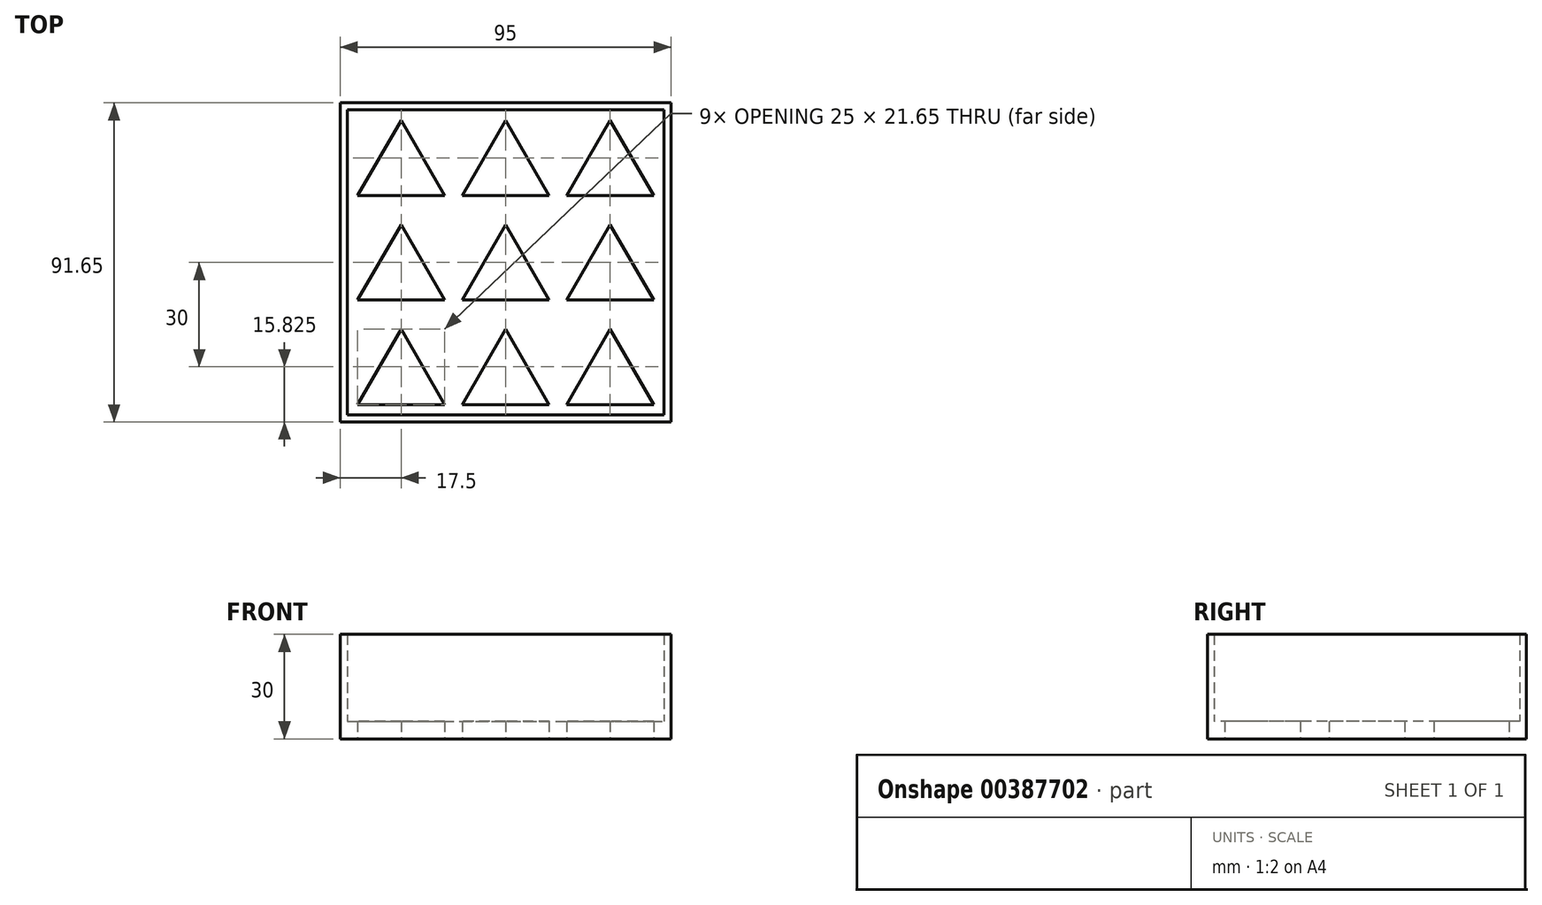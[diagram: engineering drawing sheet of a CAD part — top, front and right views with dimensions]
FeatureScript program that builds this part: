
annotation { "Feature Type Name" : "Feature", "Feature Type Description" : "" }
export const myFeature = defineFeature(function(context is Context, id is Id, definition is map)
    precondition{}
    {
        {
            var Q0;
            Q0=qCreatedBy(makeId("Top.planeOp"),FACE);
            var sketch = newSketch(context, id + "F0", { "sketchPlane" : qUnion([Q0])});
            skLineSegment(sketch, "E0", {"start": v(-12.5, 21.65) * mm, "end": v(-25, 0) * mm});
            skLineSegment(sketch, "E1", {"start": v(-25, 0) * mm, "end": v(0, 0) * mm});
            skLineSegment(sketch, "E2", {"start": v(0, 0) * mm, "end": v(-12.5, 21.65) * mm});
            skLineSegment(sketch, "E3.0.1.0", {"start": v(-25, 30) * mm, "end": v(0, 30) * mm});
            skLineSegment(sketch, "E3.0.1.1", {"start": v(-12.5, 51.65) * mm, "end": v(-25, 30) * mm});
            skLineSegment(sketch, "E3.0.1.2", {"start": v(0, 30) * mm, "end": v(-12.5, 51.65) * mm});
            skLineSegment(sketch, "E3.0.2.0", {"start": v(-25, 60) * mm, "end": v(0, 60) * mm});
            skLineSegment(sketch, "E3.0.2.1", {"start": v(-12.5, 81.65) * mm, "end": v(-25, 60) * mm});
            skLineSegment(sketch, "E3.0.2.2", {"start": v(0, 60) * mm, "end": v(-12.5, 81.65) * mm});
            skLineSegment(sketch, "E3.1.0.0", {"start": v(5, 0) * mm, "end": v(30, 0) * mm});
            skLineSegment(sketch, "E3.1.0.1", {"start": v(17.5, 21.65) * mm, "end": v(5, 0) * mm});
            skLineSegment(sketch, "E3.1.0.2", {"start": v(30, 0) * mm, "end": v(17.5, 21.65) * mm});
            skLineSegment(sketch, "E3.1.1.0", {"start": v(5, 30) * mm, "end": v(30, 30) * mm});
            skLineSegment(sketch, "E3.1.1.1", {"start": v(17.5, 51.65) * mm, "end": v(5, 30) * mm});
            skLineSegment(sketch, "E3.1.1.2", {"start": v(30, 30) * mm, "end": v(17.5, 51.65) * mm});
            skLineSegment(sketch, "E3.1.2.0", {"start": v(5, 60) * mm, "end": v(30, 60) * mm});
            skLineSegment(sketch, "E3.1.2.1", {"start": v(17.5, 81.65) * mm, "end": v(5, 60) * mm});
            skLineSegment(sketch, "E3.1.2.2", {"start": v(30, 60) * mm, "end": v(17.5, 81.65) * mm});
            skLineSegment(sketch, "E3.2.0.0", {"start": v(35, 0) * mm, "end": v(60, 0) * mm});
            skLineSegment(sketch, "E3.2.0.1", {"start": v(47.5, 21.65) * mm, "end": v(35, 0) * mm});
            skLineSegment(sketch, "E3.2.0.2", {"start": v(60, 0) * mm, "end": v(47.5, 21.65) * mm});
            skLineSegment(sketch, "E3.2.1.0", {"start": v(35, 30) * mm, "end": v(60, 30) * mm});
            skLineSegment(sketch, "E3.2.1.1", {"start": v(47.5, 51.65) * mm, "end": v(35, 30) * mm});
            skLineSegment(sketch, "E3.2.1.2", {"start": v(60, 30) * mm, "end": v(47.5, 51.65) * mm});
            skLineSegment(sketch, "E3.2.2.0", {"start": v(35, 60) * mm, "end": v(60, 60) * mm});
            skLineSegment(sketch, "E3.2.2.1", {"start": v(47.5, 81.65) * mm, "end": v(35, 60) * mm});
            skLineSegment(sketch, "E3.2.2.2", {"start": v(60, 60) * mm, "end": v(47.5, 81.65) * mm});
            skLineSegment(sketch, "E3.direction1", {"start": v(-25, 0) * mm, "end": v(5, 0) * mm, "construction": true});
            skLineSegment(sketch, "E3.direction2", {"start": v(-25, 0) * mm, "end": v(-25, 30) * mm, "construction": true});
            skLineSegment(sketch, "E4.bottom", {"start": v(-30, 86.65) * mm, "end": v(65, 86.65) * mm});
            skLineSegment(sketch, "E4.top", {"start": v(-30, -5) * mm, "end": v(65, -5) * mm});
            skLineSegment(sketch, "E4.left", {"start": v(-30, 86.65) * mm, "end": v(-30, -5) * mm});
            skLineSegment(sketch, "E4.right", {"start": v(65, 86.65) * mm, "end": v(65, -5) * mm});
            skSolve(sketch);
        }
        {
            var Q0;
            Q0 = qSketchRegion(id + "F0", true);
            extrude(context, id + "F1", {"entities" : qUnion([Q0]), "depth" : 5 * mm});
        }
        {
            var Q0;
            Q0=makeQuery(id+"F1.opExtrude","CAP_FACE",FACE,{"disambiguationData":[OSD([sQuery(id+"F0.wireOp",EDGE,"E0"),sQuery(id+"F0.wireOp",EDGE,"E1"),sQuery(id+"F0.wireOp",EDGE,"E2"),sQuery(id+"F0.wireOp",EDGE,"E3.0.1.0"),sQuery(id+"F0.wireOp",EDGE,"E3.0.1.1"),sQuery(id+"F0.wireOp",EDGE,"E3.0.1.2"),sQuery(id+"F0.wireOp",EDGE,"E3.0.2.0"),sQuery(id+"F0.wireOp",EDGE,"E3.0.2.1"),sQuery(id+"F0.wireOp",EDGE,"E3.0.2.2"),sQuery(id+"F0.wireOp",EDGE,"E3.1.0.0"),sQuery(id+"F0.wireOp",EDGE,"E3.1.0.1"),sQuery(id+"F0.wireOp",EDGE,"E3.1.0.2"),sQuery(id+"F0.wireOp",EDGE,"E3.1.1.0"),sQuery(id+"F0.wireOp",EDGE,"E3.1.1.1"),sQuery(id+"F0.wireOp",EDGE,"E3.1.1.2"),sQuery(id+"F0.wireOp",EDGE,"E3.1.2.0"),sQuery(id+"F0.wireOp",EDGE,"E3.1.2.1"),sQuery(id+"F0.wireOp",EDGE,"E3.1.2.2"),sQuery(id+"F0.wireOp",EDGE,"E3.2.0.0"),sQuery(id+"F0.wireOp",EDGE,"E3.2.0.1"),sQuery(id+"F0.wireOp",EDGE,"E3.2.0.2"),sQuery(id+"F0.wireOp",EDGE,"E3.2.1.0"),sQuery(id+"F0.wireOp",EDGE,"E3.2.1.1"),sQuery(id+"F0.wireOp",EDGE,"E3.2.1.2"),sQuery(id+"F0.wireOp",EDGE,"E3.2.2.0"),sQuery(id+"F0.wireOp",EDGE,"E3.2.2.1"),sQuery(id+"F0.wireOp",EDGE,"E3.2.2.2"),sQuery(id+"F0.wireOp",EDGE,"E4.bottom"),sQuery(id+"F0.wireOp",EDGE,"E4.top"),sQuery(id+"F0.wireOp",EDGE,"E4.left"),sQuery(id+"F0.wireOp",EDGE,"E4.right")])],"isStart":false});
            var sketch = newSketch(context, id + "F2", { "sketchPlane" : qUnion([Q0])});
            skLineSegment(sketch, "E5.0", {"start": v(-28, 84.65) * mm, "end": v(-28, -3) * mm});
            skLineSegment(sketch, "E5.1", {"start": v(63, 84.65) * mm, "end": v(-28, 84.65) * mm});
            skLineSegment(sketch, "E5.2", {"start": v(63, -3) * mm, "end": v(63, 84.65) * mm});
            skLineSegment(sketch, "E5.3", {"start": v(-28, -3) * mm, "end": v(63, -3) * mm});
            skSolve(sketch);
        }
        {
            var Q0;
            Q0=makeQuery(id+"F2.imprint","IMPRINT",FACE,{"disambiguationData":[TD([[makeQuery(id+"F2.imprint","IMPRINT",EDGE,{"derivedFrom":sQuery(id+"F2.wireOp",EDGE,"E5.0")}),-1.0]])]});
            extrude(context, id + "F3", {"entities" : qUnion([Q0]), "operationType" : NewBodyOperationType.ADD, "depth" : 25 * mm});
        }
    });
